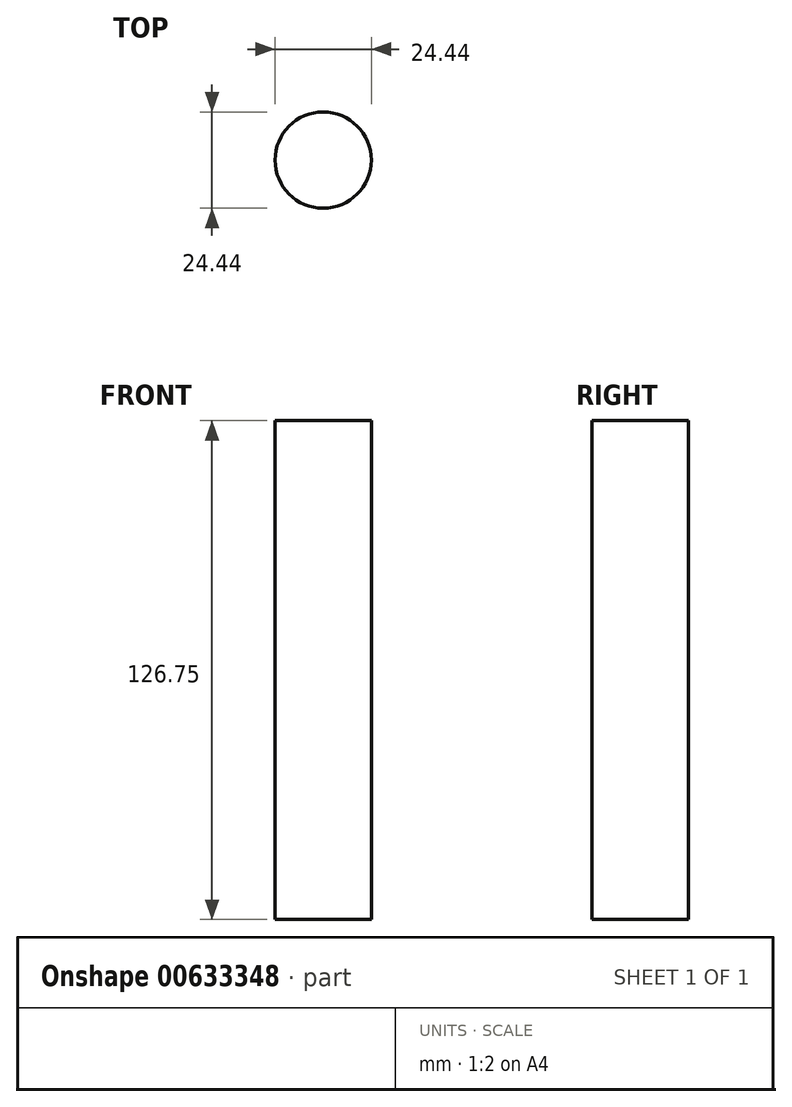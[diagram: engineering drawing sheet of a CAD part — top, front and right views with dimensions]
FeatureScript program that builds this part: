
annotation { "Feature Type Name" : "Feature", "Feature Type Description" : "" }
export const myFeature = defineFeature(function(context is Context, id is Id, definition is map)
    precondition{}
    {
        {
            var Q0;
            Q0=qCreatedBy(makeId("Top.planeOp"),FACE);
            var sketch = newSketch(context, id + "F0", { "sketchPlane" : qUnion([Q0])});
            skCircle(sketch, "E0", {"center": v(0, 0) * mm, "radius": 12.22 * mm});
            skSolve(sketch);
        }
        {
            var Q0;
            Q0 = qSketchRegion(id + "F0", true);
            extrude(context, id + "F1", {"entities" : qUnion([Q0]), "depth" : 126.75 * mm, "offsetDistance" : 25.4 * mm});
        }
    });
